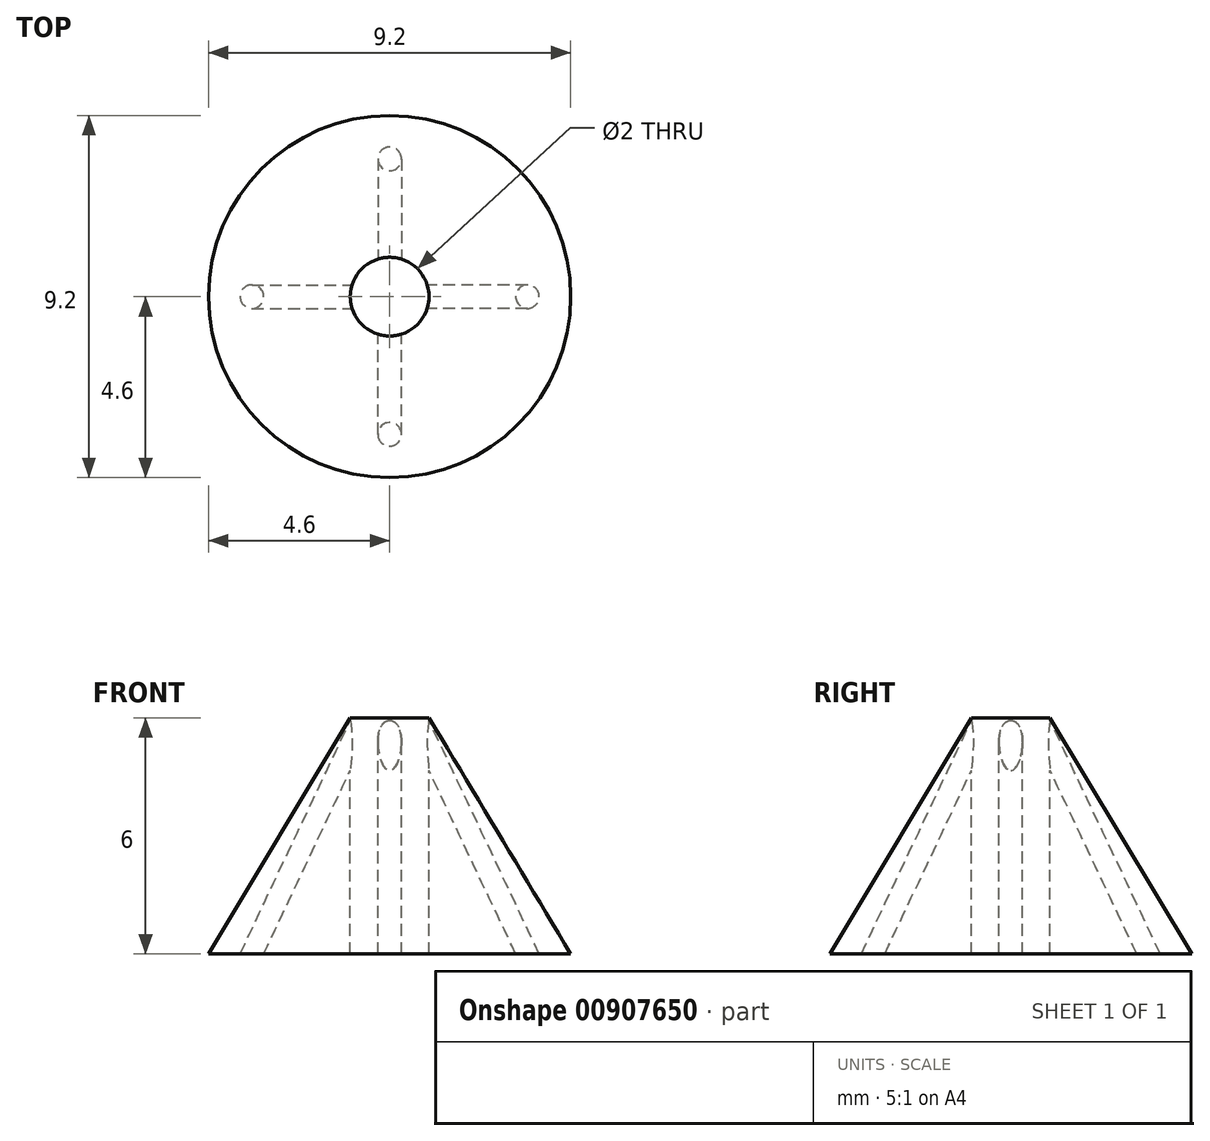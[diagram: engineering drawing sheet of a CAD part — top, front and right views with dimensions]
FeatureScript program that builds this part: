
annotation { "Feature Type Name" : "Feature", "Feature Type Description" : "" }
export const myFeature = defineFeature(function(context is Context, id is Id, definition is map)
    precondition{}
    {
        {
            var Q0;
            Q0=qCreatedBy(makeId("Front.planeOp"),FACE);
            var sketch = newSketch(context, id + "F0", { "sketchPlane" : qUnion([Q0])});
            skLineSegment(sketch, "E0", {"start": v(-1, 6) * mm, "end": v(-1, 0) * mm});
            skLineSegment(sketch, "E1", {"start": v(-1, 0) * mm, "end": v(-4.6, 0) * mm});
            skLineSegment(sketch, "E2", {"start": v(-4.6, 0) * mm, "end": v(-1, 6) * mm});
            skLineSegment(sketch, "E3", {"start": v(-1, 6) * mm, "end": v(0, 6) * mm, "construction": true});
            skLineSegment(sketch, "E4", {"start": v(0, 6) * mm, "end": v(0, 0) * mm, "construction": true});
            skLineSegment(sketch, "E5", {"start": v(0, 0) * mm, "end": v(-1, 0) * mm, "construction": true});
            skLineSegment(sketch, "E6", {"start": v(-3.83, 0) * mm, "end": v(-1, 6) * mm});
            skSolve(sketch);
        }
        {
            var Q0;
            Q0=makeQuery(id+"F0.imprint","IMPRINT",FACE,{"disambiguationData":[TD([[makeQuery(id+"F0.imprint","IMPRINT",EDGE,{"derivedFrom":sQuery(id+"F0.wireOp",EDGE,"E0")}),-1.0]])]});
            var Q1;
            {var subQ0=sQuery(id+"F0.wireOp",EDGE,"E2");Q1=makeQuery(id+"F0.imprint","IMPRINT",FACE,{"disambiguationData":[TD([[makeQuery(id+"F0.imprint","IMPRINT",EDGE,{"derivedFrom":subQ0}),-1.0]])]});}
            var Q2;
            Q2=sQuery(id+"F0.wireOp",EDGE,"E4");
            revolve(context, id + "F1", {"surfaceOperationType" : NewSurfaceOperationType.NEW, "entities" : qUnion([Q0, Q1]), "axis" : qUnion([Q2]), "revolveType" : RevolveType.FULL});
        }
        {
            var Q0;
            Q0=makeQuery(id+"F1.opRevolve","SWEPT_FACE",FACE,{"disambiguationData":[OSD([sQuery(id+"F0.wireOp",EDGE,"E1")])]});
            var sketch = newSketch(context, id + "F2", { "sketchPlane" : qUnion([Q0])});
            skCircle(sketch, "E7", {"center": v(-3.5, 0) * mm, "radius": 0.3 * mm});
            skSolve(sketch);
        }
        {
            var Q0;
            Q0=makeQuery(id+"F2.imprint","IMPRINT",FACE,{"disambiguationData":[TD([[makeQuery(id+"F2.imprint","IMPRINT",EDGE,{"derivedFrom":sQuery(id+"F2.wireOp",EDGE,"E7")}),1.0]])]});
            var Q1;
            Q1=sQuery(id+"F0.wireOp",EDGE,"E6");
            sweep(context, id + "F3", {"operationType" : NewBodyOperationType.REMOVE, "profiles" : qUnion([Q0]), "path" : qUnion([Q1])});
        }
        {
            var Q0;
            Q0=makeQuery(id+"F3.boolean.opBoolean","COPY",FACE,{"derivedFrom":makeQuery(id+"F3.opSweep","SWEPT_FACE",FACE,{"disambiguationData":[OSD([sQuery(id+"F0.wireOp",EDGE,"E2"),sQuery(id+"F2.wireOp",EDGE,"E7")])]})});
            var Q1;
            Q1=makeQuery(id+"F1.opRevolve","SWEPT_EDGE",EDGE,{"disambiguationData":[OSD([sQuery(id+"F0.wireOp",EDGE,"E0"),sQuery(id+"F0.wireOp",EDGE,"E1")])]});
            circularPattern(context, id + "F4", {"patternType" : PatternType.FACE, "faces" : qUnion([Q0]), "axis" : qUnion([Q1]), "angle" : 360 * degree, "instanceCount" : 4, "equalSpace" : true});
        }
    });
